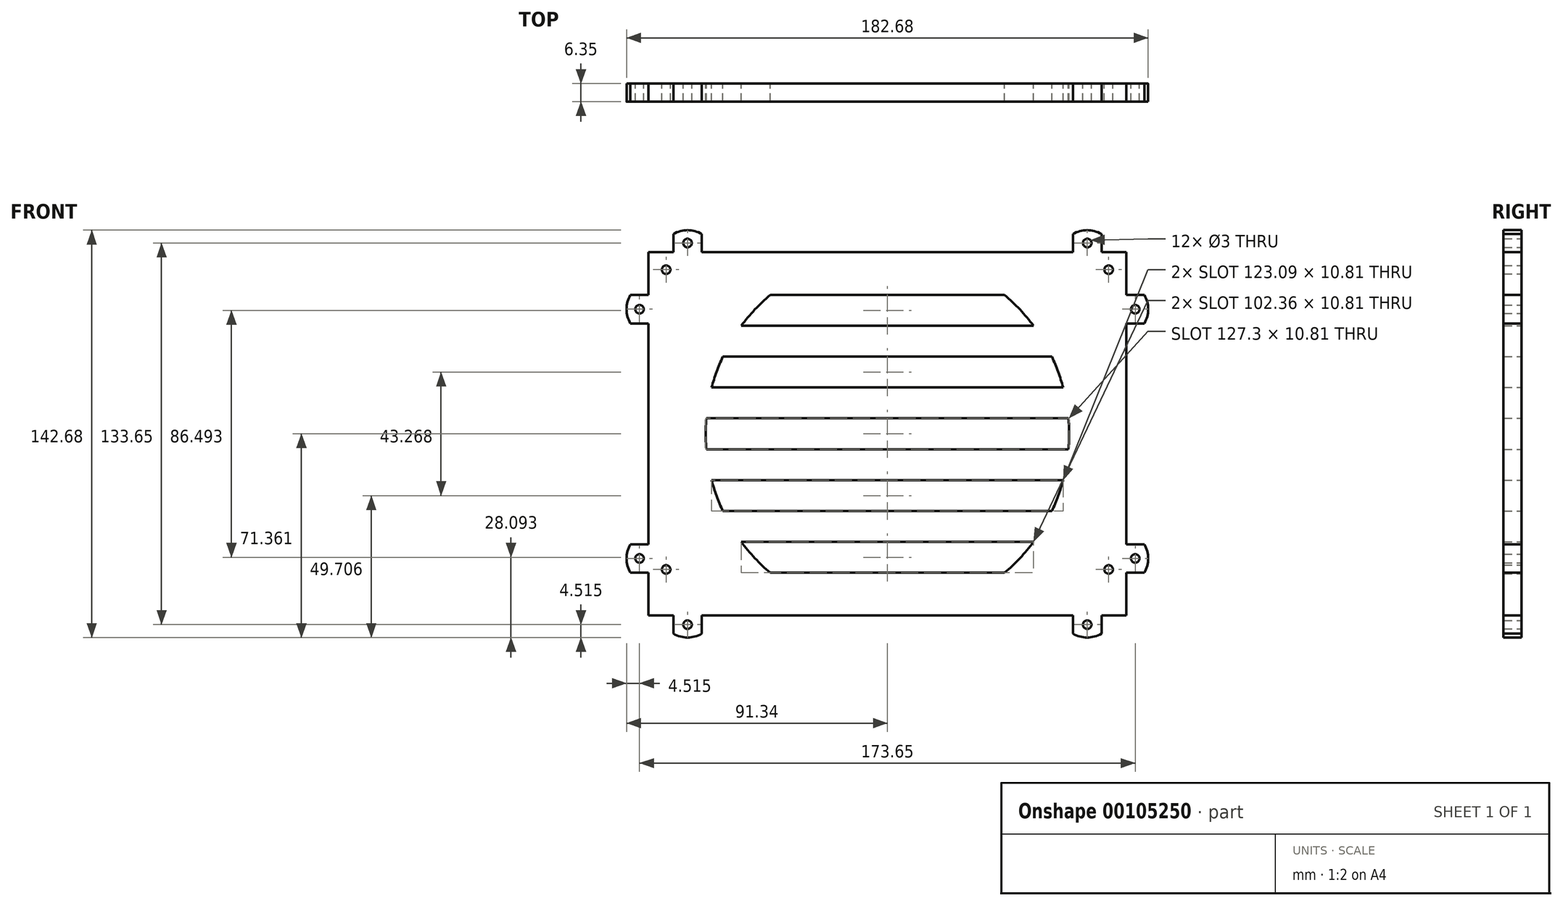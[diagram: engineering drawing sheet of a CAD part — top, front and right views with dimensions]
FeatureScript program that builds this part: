
annotation { "Feature Type Name" : "Feature", "Feature Type Description" : "" }
export const myFeature = defineFeature(function(context is Context, id is Id, definition is map)
    precondition{}
    {
        {
            var Q0;
            Q0=qCreatedBy(makeId("Front.planeOp"),FACE);
            var sketch = newSketch(context, id + "F0", { "sketchPlane" : qUnion([Q0])});
            skLineSegment(sketch, "E0.bottom", {"start": v(0, 0) * mm, "end": v(8.65, 0) * mm});
            skLineSegment(sketch, "E0.top", {"start": v(0, 127.3) * mm, "end": v(8.65, 127.3) * mm});
            skLineSegment(sketch, "E0.left", {"start": v(0, 0) * mm, "end": v(0, 15) * mm});
            skLineSegment(sketch, "E0.right", {"start": v(167.3, 0) * mm, "end": v(167.3, 15) * mm});
            skLineSegment(sketch, "E1.trimOffspring", {"start": v(0, 112.3) * mm, "end": v(0, 127.3) * mm});
            skLineSegment(sketch, "E2.trimOffspring", {"start": v(0, 25) * mm, "end": v(0, 102.3) * mm});
            skLineSegment(sketch, "E3.trimOffspring", {"start": v(18.65, 127.3) * mm, "end": v(148.65, 127.3) * mm});
            skLineSegment(sketch, "E4.trimOffspring", {"start": v(158.65, 127.3) * mm, "end": v(167.3, 127.3) * mm});
            skLineSegment(sketch, "E5", {"start": v(83.65, 127.3) * mm, "end": v(83.65, 0) * mm, "construction": true});
            skLineSegment(sketch, "E6.MirrorCS", {"start": v(167.3, 25) * mm, "end": v(167.3, 102.3) * mm});
            skLineSegment(sketch, "E7.trimOffspring", {"start": v(167.3, 112.3) * mm, "end": v(167.3, 127.3) * mm});
            skLineSegment(sketch, "E8", {"start": v(0, 63.65) * mm, "end": v(167.3, 63.65) * mm, "construction": true});
            skLineSegment(sketch, "E9.MirrorCS", {"start": v(18.65, 0) * mm, "end": v(148.65, 0) * mm});
            skLineSegment(sketch, "E10.trimOffspring", {"start": v(158.65, 0) * mm, "end": v(167.3, 0) * mm});
            skLineSegment(sketch, "E11", {"start": v(42.6, 112.3) * mm, "end": v(124.7, 112.3) * mm});
            skLineSegment(sketch, "E12", {"start": v(147.3, 112.3) * mm, "end": v(147.3, 69.03) * mm, "construction": true});
            skLineSegment(sketch, "E13.0.1.0", {"start": v(32.47, 101.5) * mm, "end": v(134.83, 101.5) * mm});
            skLineSegment(sketch, "E13.0.2.0", {"start": v(26.03, 90.69) * mm, "end": v(141.27, 90.69) * mm});
            skLineSegment(sketch, "E13.0.2.2", {"start": v(145.2, 47.42) * mm, "end": v(22.1, 47.42) * mm});
            skLineSegment(sketch, "E13.0.3.0", {"start": v(22.1, 79.88) * mm, "end": v(145.2, 79.88) * mm});
            skLineSegment(sketch, "E13.0.3.2", {"start": v(141.27, 36.61) * mm, "end": v(26.03, 36.61) * mm});
            skLineSegment(sketch, "E13.0.4.0", {"start": v(20, 69.07) * mm, "end": v(147.07, 69.07) * mm});
            skLineSegment(sketch, "E13.0.4.2", {"start": v(134.83, 25.8) * mm, "end": v(32.47, 25.8) * mm});
            skLineSegment(sketch, "E13.direction1", {"start": v(20.23, 69.03) * mm, "end": v(45, 69.03) * mm, "construction": true});
            skLineSegment(sketch, "E13.direction2", {"start": v(20, 69.03) * mm, "end": v(20, 58.23) * mm, "construction": true});
            skLineSegment(sketch, "E14", {"start": v(66.95, 127.3) * mm, "end": v(66.95, 112.3) * mm, "construction": true});
            skLineSegment(sketch, "E15.0.0.5", {"start": v(20.23, 58.27) * mm, "end": v(147.07, 58.27) * mm});
            skLineSegment(sketch, "E15.6.0.5", {"start": v(124.7, 15) * mm, "end": v(42.6, 15) * mm});
            skLineSegment(sketch, "E16", {"start": v(70.23, 15) * mm, "end": v(70.23, 0) * mm, "construction": true});
            skLineSegment(sketch, "E17.MirrorCS", {"start": v(8.65, 127.3) * mm, "end": v(8.65, 133.65) * mm});
            skLineSegment(sketch, "E18.MirrorCS", {"start": v(18.65, 127.3) * mm, "end": v(18.65, 133.65) * mm});
            skLineSegment(sketch, "E19.MirrorCS", {"start": v(158.65, 0) * mm, "end": v(158.65, -6.29) * mm});
            skArc(sketch, "E20", {"start": v(42.6, 112.3) * mm, "mid": v(37.22, 107.2) * mm, "end": v(32.47, 101.5) * mm});
            skPoint(sketch, "E21.orphan", {"position": v(20, 101.5) * mm});
            skPoint(sketch, "E22.orphan", {"position": v(20, 25.8) * mm});
            skPoint(sketch, "E23.orphan", {"position": v(20, 58.27) * mm});
            skPoint(sketch, "E24.orphan", {"position": v(20, 15) * mm});
            skArc(sketch, "E25.trimOffspring", {"start": v(124.7, 15) * mm, "mid": v(130.08, 20.1) * mm, "end": v(134.83, 25.8) * mm});
            skPoint(sketch, "E26.orphan", {"position": v(147.3, 58.27) * mm});
            skPoint(sketch, "E27.orphan", {"position": v(147.3, 69.07) * mm});
            skPoint(sketch, "E28.orphan", {"position": v(147.3, 90.69) * mm});
            skPoint(sketch, "E29.orphan", {"position": v(147.3, 58.23) * mm});
            skPoint(sketch, "E30.orphan", {"position": v(147.3, 101.5) * mm});
            skPoint(sketch, "E31.orphan", {"position": v(147.3, 47.42) * mm});
            skPoint(sketch, "E32.orphan", {"position": v(20, 90.69) * mm});
            skPoint(sketch, "E33.orphan", {"position": v(20, 47.42) * mm});
            skArc(sketch, "E34.trimOffspring", {"start": v(26.03, 90.69) * mm, "mid": v(23.82, 85.37) * mm, "end": v(22.1, 79.88) * mm});
            skArc(sketch, "E35.trimOffspring", {"start": v(20.23, 69.07) * mm, "mid": v(20, 63.67) * mm, "end": v(20.23, 58.27) * mm});
            skArc(sketch, "E36.trimOffspring", {"start": v(22.1, 47.42) * mm, "mid": v(23.82, 41.93) * mm, "end": v(26.03, 36.61) * mm});
            skArc(sketch, "E37.trimOffspring", {"start": v(141.27, 36.61) * mm, "mid": v(143.48, 41.93) * mm, "end": v(145.2, 47.42) * mm});
            skArc(sketch, "E38.trimOffspring", {"start": v(147.07, 58.27) * mm, "mid": v(147.3, 63.67) * mm, "end": v(147.07, 69.07) * mm});
            skArc(sketch, "E39", {"start": v(18.65, 133.65) * mm, "mid": v(13.65, 134.99) * mm, "end": v(8.65, 133.65) * mm});
            skLineSegment(sketch, "E40", {"start": v(8.65, 130.47) * mm, "end": v(18.65, 130.47) * mm, "construction": true});
            skCircle(sketch, "E41", {"center": v(13.65, 130.47) * mm, "radius": 1.5 * mm});
            skLineSegment(sketch, "E42.MirrorCS", {"start": v(158.65, 127.3) * mm, "end": v(158.65, 133.65) * mm});
            skLineSegment(sketch, "E43.MirrorCS", {"start": v(148.65, 127.3) * mm, "end": v(148.65, 133.65) * mm});
            skCircle(sketch, "E44.MirrorC", {"center": v(153.65, 130.47) * mm, "radius": 1.5 * mm});
            skArc(sketch, "E45.MirrorCS", {"start": v(148.65, 133.65) * mm, "mid": v(153.65, 134.99) * mm, "end": v(158.65, 133.65) * mm});
            skArc(sketch, "E46.MirrorCS", {"start": v(148.65, -6.35) * mm, "mid": v(153.65, -7.69) * mm, "end": v(158.65, -6.35) * mm});
            skLineSegment(sketch, "E47.MirrorCS", {"start": v(148.65, 0) * mm, "end": v(148.65, -6.35) * mm});
            skCircle(sketch, "E48.MirrorC", {"center": v(153.65, -3.18) * mm, "radius": 1.5 * mm});
            skLineSegment(sketch, "E49.MirrorCS", {"start": v(158.65, 0) * mm, "end": v(158.65, -6.35) * mm});
            skCircle(sketch, "E50.MirrorC", {"center": v(13.65, -3.18) * mm, "radius": 1.5 * mm});
            skLineSegment(sketch, "E51.MirrorCS", {"start": v(8.65, 0) * mm, "end": v(8.65, -6.35) * mm});
            skLineSegment(sketch, "E52.MirrorCS", {"start": v(18.65, 0) * mm, "end": v(18.65, -6.35) * mm});
            skArc(sketch, "E53.MirrorCS", {"start": v(18.65, -6.35) * mm, "mid": v(13.65, -7.69) * mm, "end": v(8.65, -6.35) * mm});
            skLineSegment(sketch, "E54", {"start": v(0, 112.3) * mm, "end": v(-6.35, 112.3) * mm});
            skLineSegment(sketch, "E55", {"start": v(0, 102.3) * mm, "end": v(-6.35, 102.3) * mm});
            skArc(sketch, "E56", {"start": v(-6.35, 112.3) * mm, "mid": v(-7.69, 107.3) * mm, "end": v(-6.35, 102.3) * mm});
            skLineSegment(sketch, "E57", {"start": v(-3.18, 112.3) * mm, "end": v(-3.18, 102.3) * mm, "construction": true});
            skCircle(sketch, "E58", {"center": v(-3.18, 107.3) * mm, "radius": 1.5 * mm});
            skArc(sketch, "E59.MirrorCS", {"start": v(-6.35, 15) * mm, "mid": v(-7.69, 20) * mm, "end": v(-6.35, 25) * mm});
            skLineSegment(sketch, "E60.MirrorCS", {"start": v(0, 15) * mm, "end": v(-6.35, 15) * mm});
            skLineSegment(sketch, "E61.MirrorCS", {"start": v(0, 25) * mm, "end": v(-6.35, 25) * mm});
            skCircle(sketch, "E62.MirrorC", {"center": v(-3.17, 20) * mm, "radius": 1.5 * mm});
            skLineSegment(sketch, "E63.MirrorCS", {"start": v(167.3, 112.3) * mm, "end": v(173.65, 112.3) * mm});
            skLineSegment(sketch, "E64.MirrorCS", {"start": v(167.3, 102.3) * mm, "end": v(173.65, 102.3) * mm});
            skCircle(sketch, "E65.MirrorC", {"center": v(170.48, 107.3) * mm, "radius": 1.5 * mm});
            skCircle(sketch, "E66.MirrorC", {"center": v(170.48, 20) * mm, "radius": 1.5 * mm});
            skArc(sketch, "E67.MirrorCS", {"start": v(173.65, 15) * mm, "mid": v(174.99, 20) * mm, "end": v(173.65, 25) * mm});
            skLineSegment(sketch, "E68.MirrorCS", {"start": v(167.3, 15) * mm, "end": v(173.65, 15) * mm});
            skLineSegment(sketch, "E69.MirrorCS", {"start": v(167.3, 25) * mm, "end": v(173.65, 25) * mm});
            skArc(sketch, "E70.MirrorCS", {"start": v(173.65, 112.3) * mm, "mid": v(174.99, 107.3) * mm, "end": v(173.65, 102.3) * mm});
            skPoint(sketch, "E71.orphan", {"position": v(147.3, 36.61) * mm});
            skPoint(sketch, "E72.orphan", {"position": v(20, 36.61) * mm});
            skArc(sketch, "E73.trimOffspring", {"start": v(134.83, 101.5) * mm, "mid": v(130.08, 107.2) * mm, "end": v(124.7, 112.3) * mm});
            skArc(sketch, "E74.trimOffspring", {"start": v(145.2, 79.88) * mm, "mid": v(143.48, 85.37) * mm, "end": v(141.27, 90.69) * mm});
            skArc(sketch, "E75.trimOffspring", {"start": v(32.47, 25.8) * mm, "mid": v(37.22, 20.1) * mm, "end": v(42.6, 15) * mm});
            skArc(sketch, "E76.trimOffspring", {"start": v(20.23, 69.07) * mm, "mid": v(20, 64.57) * mm, "end": v(20.1, 60.06) * mm});
            skPoint(sketch, "E77.orphan", {"position": v(20, 79.88) * mm});
            skPoint(sketch, "E78.orphan", {"position": v(147.3, 79.88) * mm});
            skLineSegment(sketch, "E79.0", {"start": v(18.65, 127.06) * mm, "end": v(148.65, 127.06) * mm});
            skLineSegment(sketch, "E80", {"start": v(147.07, 58.27) * mm, "end": v(145.2, 47.42) * mm, "construction": true});
            skLineSegment(sketch, "E81", {"start": v(147.3, 69.07) * mm, "end": v(145.2, 79.88) * mm, "construction": true});
            skCircle(sketch, "E82", {"center": v(6.15, 121.15) * mm, "radius": 1.5 * mm});
            skCircle(sketch, "E83", {"center": v(161.15, 121.15) * mm, "radius": 1.5 * mm});
            skCircle(sketch, "E84", {"center": v(6.15, 16.15) * mm, "radius": 1.5 * mm});
            skCircle(sketch, "E85", {"center": v(161.15, 16.15) * mm, "radius": 1.5 * mm});
            skLineSegment(sketch, "E86", {"start": v(83.65, 121.15) * mm, "end": v(161.15, 121.15) * mm, "construction": true});
            skLineSegment(sketch, "E87", {"start": v(6.15, 121.15) * mm, "end": v(83.65, 121.15) * mm, "construction": true});
            skSolve(sketch);
        }
        {
            var Q0;
            Q0=makeQuery(id+"F0.imprint","IMPRINT",FACE,{"disambiguationData":[TD([[makeQuery(id+"F0.imprint","IMPRINT",EDGE,{"derivedFrom":sQuery(id+"F0.wireOp",EDGE,"E0.bottom")}),1.0]])]});
            extrude(context, id + "F1", {"entities" : qUnion([Q0]), "depth" : 6.35 * mm});
        }
    });
